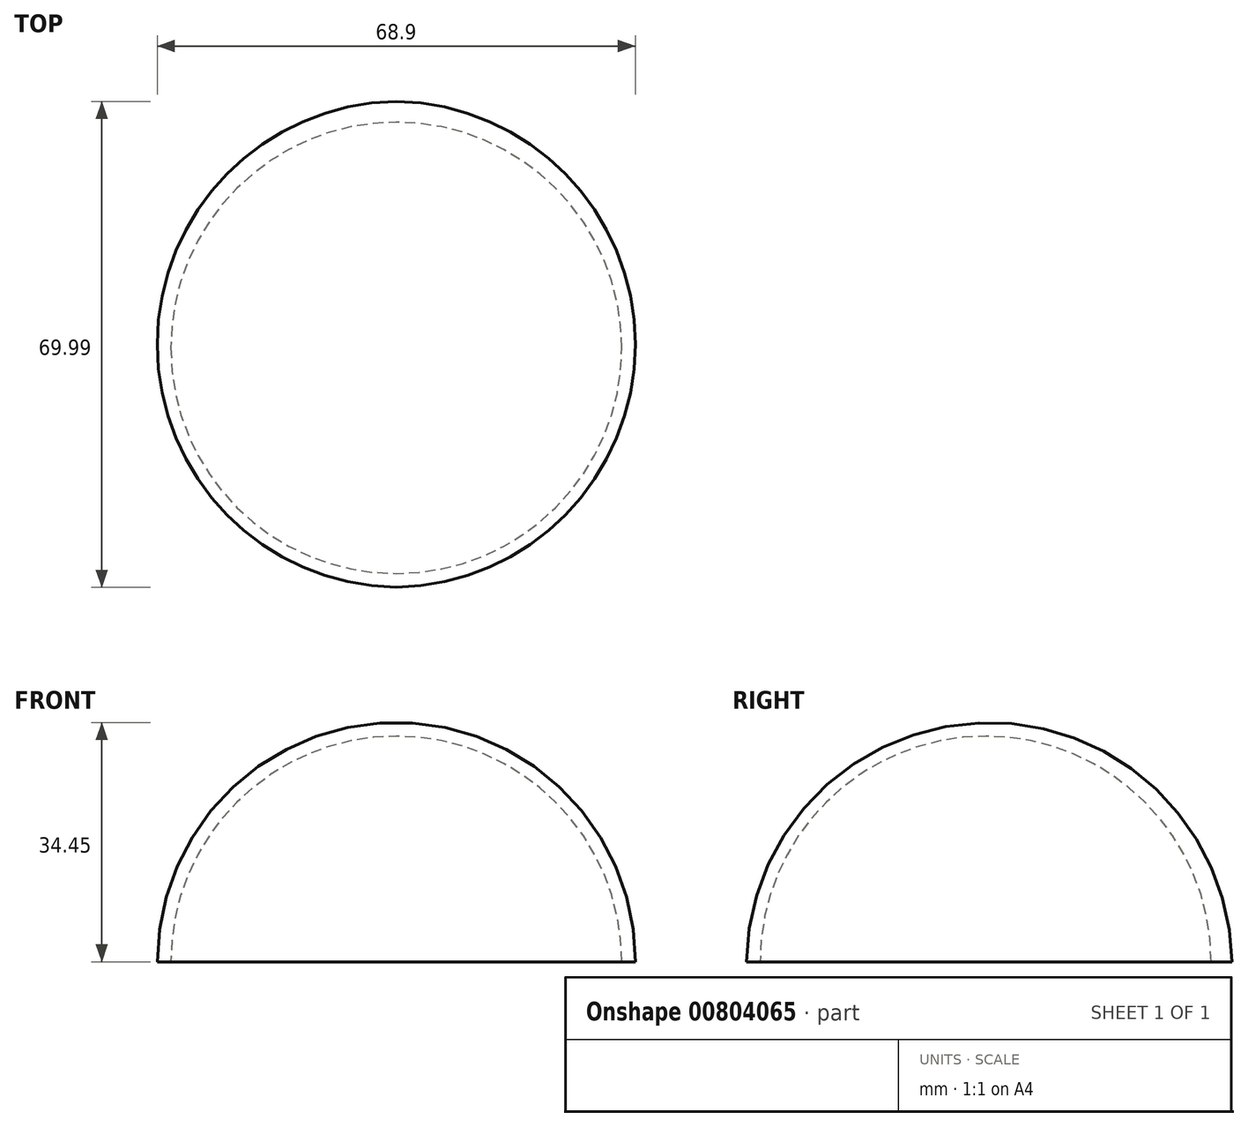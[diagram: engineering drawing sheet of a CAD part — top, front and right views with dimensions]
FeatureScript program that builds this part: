
annotation { "Feature Type Name" : "Feature", "Feature Type Description" : "" }
export const myFeature = defineFeature(function(context is Context, id is Id, definition is map)
    precondition{}
    {
        {
            var Q0;
            Q0=qCreatedBy(makeId("Top.planeOp"),FACE);
            var sketch = newSketch(context, id + "F0", { "sketchPlane" : qUnion([Q0])});
            skArc(sketch, "E0", {"start": v(0, -34.5) * mm, "mid": v(34.45, 0.5) * mm, "end": v(0, 35.5) * mm});
            skLineSegment(sketch, "E1", {"start": v(0, 35.5) * mm, "end": v(0, -34.5) * mm});
            skSolve(sketch);
        }
        {
            var Q0;
            Q0 = qSketchRegion(id + "F0", true);
            var Q1;
            Q1=sQuery(id+"F0.wireOp",EDGE,"E1");
            revolve(context, id + "F1", {"surfaceOperationType" : NewSurfaceOperationType.NEW, "entities" : qUnion([Q0]), "axis" : qUnion([Q1]), "revolveType" : RevolveType.ONE_DIRECTION, "angle" : 180 * degree});
        }
        {
            var Q0;
            Q0=makeQuery(id+"F1.opRevolve","CAP_FACE",FACE,{"disambiguationData":[OSD([sQuery(id+"F0.wireOp",EDGE,"E0"),sQuery(id+"F0.wireOp",EDGE,"E1")])],"isStart":false});
            var sketch = newSketch(context, id + "F2", { "sketchPlane" : qUnion([Q0])});
            skArc(sketch, "E2", {"start": v(32.5, 0) * mm, "mid": v(0, 32.5) * mm, "end": v(-32.5, 0) * mm});
            skLineSegment(sketch, "E3", {"start": v(0, 0) * mm, "end": v(32.5, 0) * mm});
            skLineSegment(sketch, "E4", {"start": v(0, 0) * mm, "end": v(-32.5, 0) * mm});
            skSolve(sketch);
        }
        {
            var Q0;
            Q0 = qSketchRegion(id + "F2", true);
            var Q1;
            Q1=sQuery(id+"F2.wireOp",EDGE,"E3");
            revolve(context, id + "F3", {"operationType" : NewBodyOperationType.REMOVE, "surfaceOperationType" : NewSurfaceOperationType.NEW, "entities" : qUnion([Q0]), "axis" : qUnion([Q1]), "revolveType" : RevolveType.FULL, "oppositeDirection" : true});
        }
    });
